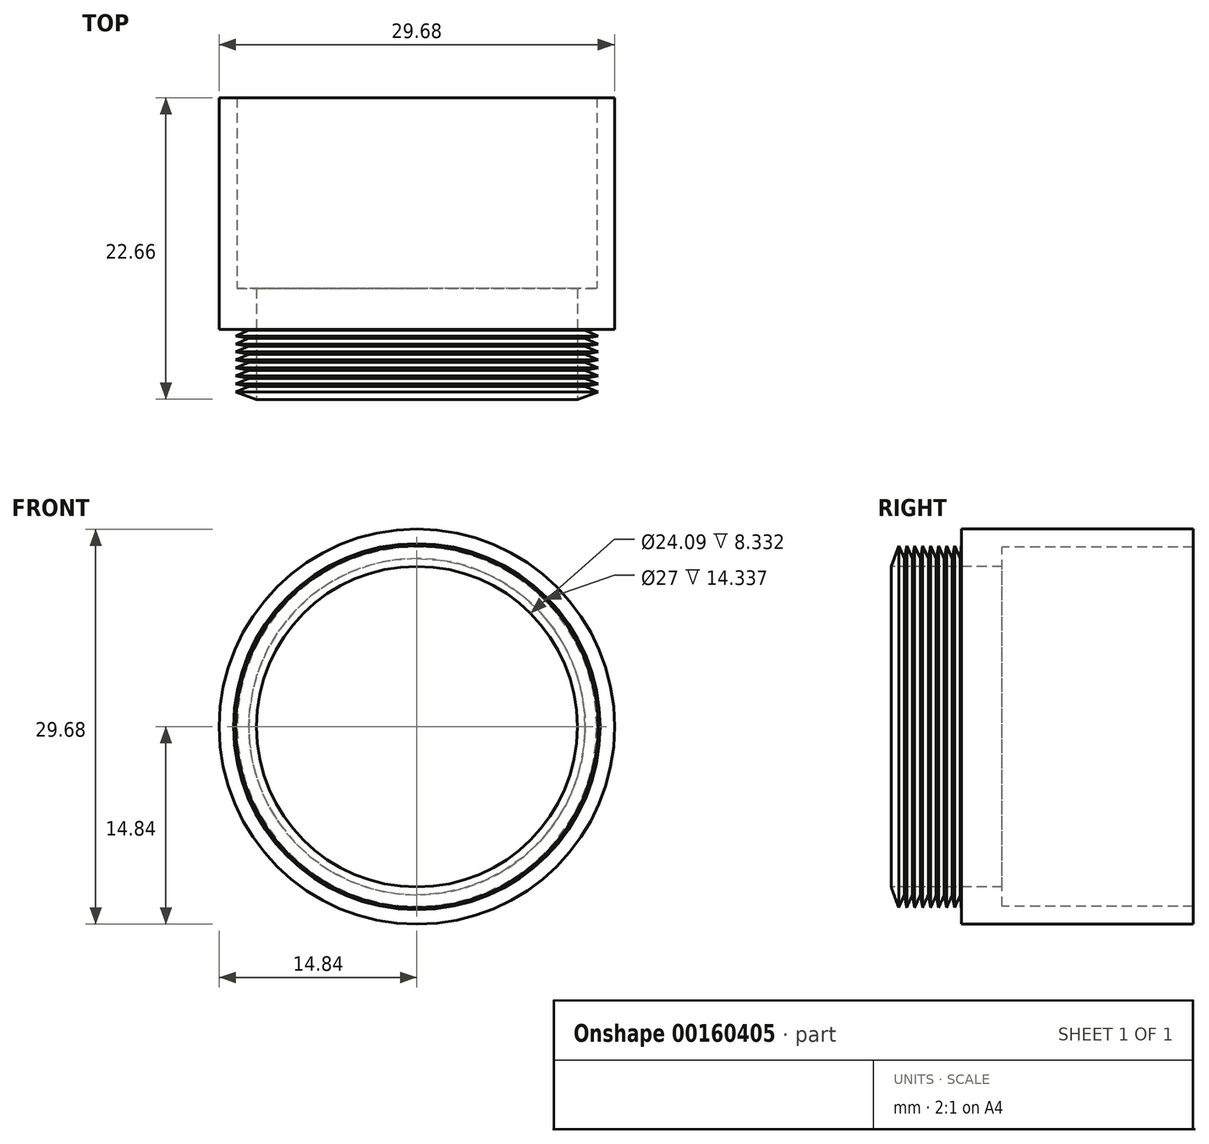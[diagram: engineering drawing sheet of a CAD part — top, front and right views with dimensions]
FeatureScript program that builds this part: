
annotation { "Feature Type Name" : "Feature", "Feature Type Description" : "" }
export const myFeature = defineFeature(function(context is Context, id is Id, definition is map)
    precondition{}
    {
        {
            var Q0;
            Q0=qCreatedBy(makeId("Right.planeOp"),FACE);
            var sketch = newSketch(context, id + "F0", { "sketchPlane" : qUnion([Q0])});
            skLineSegment(sketch, "E0", {"start": v(-0.56, 12.05) * mm, "end": v(7.77, 12.05) * mm});
            skLineSegment(sketch, "E1", {"start": v(7.77, 12.05) * mm, "end": v(7.77, 13.5) * mm});
            skLineSegment(sketch, "E2", {"start": v(7.77, 13.5) * mm, "end": v(22.1, 13.5) * mm});
            skLineSegment(sketch, "E3", {"start": v(22.1, 13.5) * mm, "end": v(22.1, 14.84) * mm});
            skLineSegment(sketch, "E4", {"start": v(22.1, 14.84) * mm, "end": v(4.71, 14.84) * mm});
            skLineSegment(sketch, "E5", {"start": v(4.71, 14.84) * mm, "end": v(4.71, 13.76) * mm});
            skLineSegment(sketch, "E6", {"start": v(0, 0) * mm, "end": v(28.3, 0) * mm});
            skLineSegment(sketch, "E7", {"start": v(-0.56, 12.05) * mm, "end": v(0, 13.6) * mm});
            skLineSegment(sketch, "E8", {"start": v(0, 13.6) * mm, "end": v(0.42, 12.63) * mm});
            skLineSegment(sketch, "E9.2.0.0", {"start": v(0.6, 13.6) * mm, "end": v(1.02, 12.63) * mm});
            skLineSegment(sketch, "E10", {"start": v(0.6, 13.6) * mm, "end": v(0.42, 12.63) * mm});
            skLineSegment(sketch, "E11.direction1", {"start": v(0.42, 12.63) * mm, "end": v(1.02, 12.63) * mm, "construction": true});
            skLineSegment(sketch, "E12.0.1.0", {"start": v(1.2, 13.6) * mm, "end": v(1.62, 12.63) * mm});
            skLineSegment(sketch, "E12.3.1.0", {"start": v(1.2, 13.6) * mm, "end": v(1.02, 12.63) * mm});
            skLineSegment(sketch, "E12.0.2.0", {"start": v(1.8, 13.6) * mm, "end": v(2.22, 12.63) * mm});
            skLineSegment(sketch, "E12.3.2.0", {"start": v(1.8, 13.6) * mm, "end": v(1.62, 12.63) * mm});
            skLineSegment(sketch, "E12.0.3.0", {"start": v(2.4, 13.6) * mm, "end": v(2.82, 12.63) * mm});
            skLineSegment(sketch, "E12.3.3.0", {"start": v(2.4, 13.6) * mm, "end": v(2.22, 12.63) * mm});
            skLineSegment(sketch, "E12.0.4.0", {"start": v(3, 13.6) * mm, "end": v(3.42, 12.63) * mm});
            skLineSegment(sketch, "E12.3.4.0", {"start": v(3, 13.6) * mm, "end": v(2.82, 12.63) * mm});
            skLineSegment(sketch, "E12.0.5.0", {"start": v(3.6, 13.6) * mm, "end": v(4.02, 12.64) * mm});
            skLineSegment(sketch, "E12.3.5.0", {"start": v(3.6, 13.6) * mm, "end": v(3.42, 12.64) * mm});
            skLineSegment(sketch, "E12.0.6.0", {"start": v(4.2, 13.6) * mm, "end": v(4.62, 12.64) * mm});
            skLineSegment(sketch, "E12.3.6.0", {"start": v(4.2, 13.6) * mm, "end": v(4.02, 12.64) * mm});
            skLineSegment(sketch, "E13", {"start": v(4.62, 12.64) * mm, "end": v(4.71, 13.76) * mm});
            skSolve(sketch);
        }
        {
            var Q0;
            Q0 = qSketchRegion(id + "F0", true);
            var Q1;
            Q1=sQuery(id+"F0.wireOp",EDGE,"E6");
            revolve(context, id + "F1", {"entities" : qUnion([Q0]), "axis" : qUnion([Q1]), "revolveType" : RevolveType.FULL});
        }
    });
